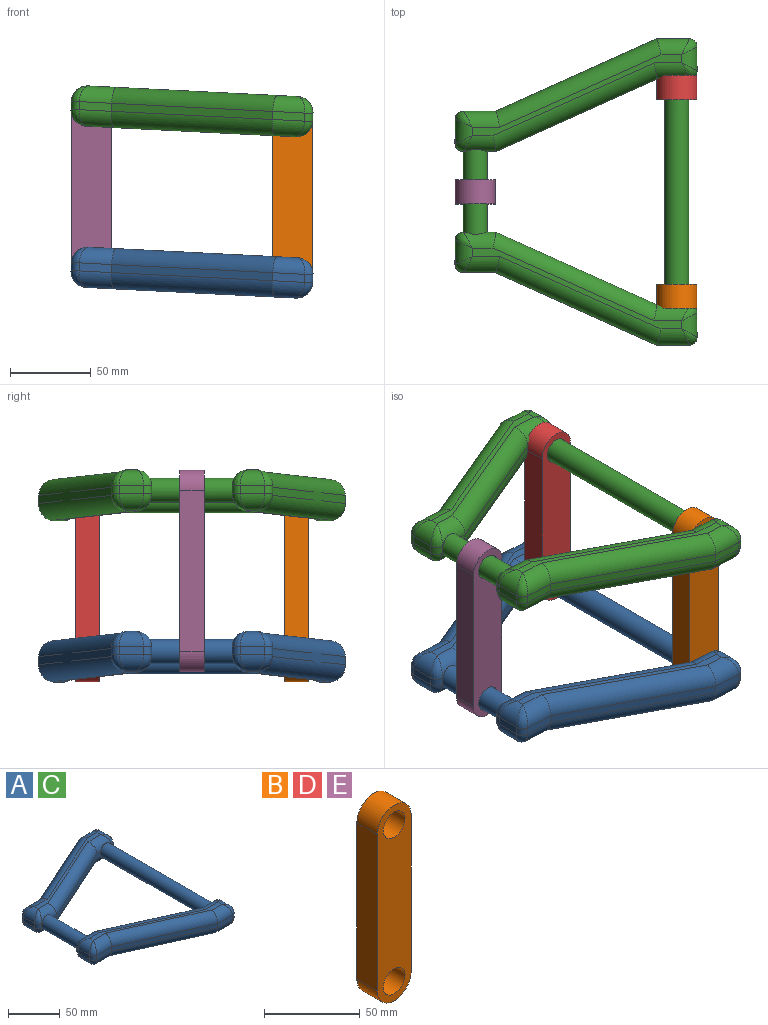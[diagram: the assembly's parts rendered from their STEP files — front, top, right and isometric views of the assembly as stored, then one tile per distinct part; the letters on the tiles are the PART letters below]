
ASSEMBLY  parts=5 mates=6
PART A: 86 faces, bbox 150x190x25 mm
  f0: plane 2.5x0.43mm, normal (0,1,0), area 0.4mm2, adj f18,f38,f84
  f1: plane 2.5x0.43mm, normal (0,1,0), area 0.4mm2, adj f19,f33,f78
  f2: plane 2.5x0.43mm, normal (0,-1,0), area 0.4mm2, adj f19,f51,f69
  f3: plane 2.5x0.43mm, normal (0,-1,0), area 0.4mm2, adj f18,f55,f63
  f4: plane 2.5x0.43mm, normal (0,-1,0), area 0.4mm2, adj f18,f47,f63
  f5: plane 5.43x5mm, normal (0,-1,0), area 25.7mm2, adj f12,f19,f51,f59
  f6: plane 2.5x0.43mm, normal (0,1,0), area 0.4mm2, adj f19,f41,f78
  f7: plane 2.5x0.43mm, normal (0,1,0), area 0.4mm2, adj f18,f37,f84
  f8: plane 100x45mm, normal (-0.41,0.91,0), area 548.3mm2, adj f9,f15,f50,f58
  f9: plane 20x5mm, normal (0,1,0), area 100mm2, adj f8,f48,f56,f66
  f10: plane 15x5mm, normal (-1,0,0), area 75mm2, adj f46,f54,f63,f66
  f11: plane 5.43x5mm, normal (0,-1,0), area 25.7mm2, adj f12,f18,f47,f55
  f12: plane 100x45mm, normal (0.41,-0.91,0), area 548.3mm2, adj f5,f11,f49,f57
  f13: plane 2.5x0.43mm, normal (0,-1,0), area 0.4mm2, adj f19,f59,f69
  f14: plane 15x5mm, normal (1,0,0), area 75mm2, adj f53,f61,f69,f72
  f15: plane 20x5mm, normal (0,1,0), area 100mm2, adj f8,f52,f60,f72
  f16: plane 130x50mm, normal (0,0,1), area 456.8mm2, adj f54,f55,f56,f57,f58,f59,f60,f61
  f17: plane 130x50mm, normal (0,0,-1), area 456.8mm2, adj f46,f47,f48,f49,f50,f51,f52,f53
  f18: cylinder r=7.5mm len=52.68mm, axis (0,1,0), area 2406.1mm2, adj f0,f3,f4,f7,f11,f23,f37,f38
  f19: cylinder r=7.5mm len=142.68mm, axis (0,1,0), area 6647.2mm2, adj f1,f2,f5,f6,f13,f25,f33,f41
  f20: plane 100x45mm, normal (-0.41,-0.91,0), area 548.3mm2, adj f21,f27,f32,f44
  f21: plane 20x5mm, normal (0,-1,0), area 100mm2, adj f20,f34,f42,f81
  f22: plane 15x5mm, normal (-1,0,0), area 75mm2, adj f36,f40,f81,f84
  f23: plane 5.43x5mm, normal (0,1,0), area 25.7mm2, adj f18,f24,f37,f38
  f24: plane 100x45mm, normal (0.41,0.91,0), area 548.3mm2, adj f23,f25,f35,f39
  f25: plane 5.43x5mm, normal (0,1,0), area 25.7mm2, adj f19,f24,f33,f41
  f26: plane 15x5mm, normal (1,0,0), area 75mm2, adj f31,f43,f75,f78
  f27: plane 20x5mm, normal (0,-1,0), area 100mm2, adj f20,f30,f45,f75
  f28: plane 130x50mm, normal (0,0,1), area 456.8mm2, adj f30,f31,f32,f33,f34,f35,f36,f37
  f29: plane 130x50mm, normal (0,0,-1), area 456.8mm2, adj f38,f39,f40,f41,f42,f43,f44,f45
  f30: cylinder r=10mm len=20mm, axis (1,0,0), area 273.4mm2, adj f27,f28,f32,f74
  f31: cylinder r=10mm len=15mm, axis (0,1,0), area 178.5mm2, adj f26,f28,f74,f77
  f32: cylinder r=10mm len=106.06mm, axis (0.91,-0.41,0), area 1722.5mm2, adj f20,f28,f30,f34
  f33: cylinder r=10mm len=22.15mm, axis (-1,0,0), area 244.6mm2, adj f1,f19,f25,f28,f35,f77
  f34: cylinder r=10mm len=22.15mm, axis (1,0,0), area 297.9mm2, adj f21,f28,f32,f80
  f35: cylinder r=10mm len=106.06mm, axis (-0.91,0.41,0), area 1722.5mm2, adj f24,f28,f33,f37
  f36: cylinder r=10mm len=15mm, axis (0,-1,0), area 178.5mm2, adj f22,f28,f80,f83
  f37: cylinder r=10mm len=20mm, axis (-1,0,0), area 220.1mm2, adj f7,f18,f23,f28,f35,f83
  f38: cylinder r=10mm len=20mm, axis (1,0,0), area 220.1mm2, adj f0,f18,f23,f29,f39,f85
  f39: cylinder r=10mm len=106.06mm, axis (0.91,-0.41,0), area 1722.5mm2, adj f24,f29,f38,f41
  f40: cylinder r=10mm len=15mm, axis (0,1,0), area 178.5mm2, adj f22,f29,f82,f85
  f41: cylinder r=10mm len=22.15mm, axis (1,0,0), area 244.6mm2, adj f6,f19,f25,f29,f39,f79
  f42: cylinder r=10mm len=22.15mm, axis (-1,0,0), area 297.9mm2, adj f21,f29,f44,f82
  f43: cylinder r=10mm len=15mm, axis (0,-1,0), area 178.5mm2, adj f26,f29,f76,f79
  f44: cylinder r=10mm len=106.06mm, axis (-0.91,0.41,0), area 1722.5mm2, adj f20,f29,f42,f45
  f45: cylinder r=10mm len=20mm, axis (-1,0,0), area 273.4mm2, adj f27,f29,f44,f76
  f46: cylinder r=10mm len=15mm, axis (0,-1,0), area 178.5mm2, adj f10,f17,f64,f67
  f47: cylinder r=10mm len=20mm, axis (1,0,0), area 220.1mm2, adj f4,f11,f17,f18,f49,f64
  f48: cylinder r=10mm len=22.15mm, axis (-1,0,0), area 297.9mm2, adj f9,f17,f50,f67
  f49: cylinder r=10mm len=106.06mm, axis (0.91,0.41,0), area 1722.5mm2, adj f12,f17,f47,f51
  f50: cylinder r=10mm len=106.06mm, axis (-0.91,-0.41,0), area 1722.5mm2, adj f8,f17,f48,f52
  f51: cylinder r=10mm len=22.15mm, axis (1,0,0), area 244.6mm2, adj f2,f5,f17,f19,f49,f70
  f52: cylinder r=10mm len=20mm, axis (-1,0,0), area 273.4mm2, adj f15,f17,f50,f73
  f53: cylinder r=10mm len=15mm, axis (0,1,0), area 178.5mm2, adj f14,f17,f70,f73
  f54: cylinder r=10mm len=15mm, axis (0,1,0), area 178.5mm2, adj f10,f16,f62,f65
  f55: cylinder r=10mm len=20mm, axis (-1,0,0), area 220.1mm2, adj f3,f11,f16,f18,f57,f62
  f56: cylinder r=10mm len=22.15mm, axis (1,0,0), area 297.9mm2, adj f9,f16,f58,f65
  f57: cylinder r=10mm len=106.06mm, axis (-0.91,-0.41,0), area 1722.5mm2, adj f12,f16,f55,f59
  f58: cylinder r=10mm len=106.06mm, axis (0.91,0.41,0), area 1722.5mm2, adj f8,f16,f56,f60
  f59: cylinder r=10mm len=22.15mm, axis (-1,0,0), area 244.6mm2, adj f5,f13,f16,f19,f57,f68
  f60: cylinder r=10mm len=20mm, axis (1,0,0), area 273.4mm2, adj f15,f16,f58,f71
  f61: cylinder r=10mm len=15mm, axis (0,-1,0), area 178.5mm2, adj f14,f16,f68,f71
  f62: bspline ~11.94x10mm, area 82.5mm2, adj f54,f55,f63
  f63: cylinder r=5mm len=5mm, axis (0,0,1), area 39.3mm2, adj f3,f4,f10,f62,f64
  f64: bspline ~11.94x10mm, area 82.5mm2, adj f46,f47,f63
  f65: bspline ~11.94x10mm, area 82.5mm2, adj f54,f56,f66
  f66: cylinder r=5mm len=5mm, axis (0,0,-1), area 39.3mm2, adj f9,f10,f65,f67
  f67: bspline ~11.94x10mm, area 82.5mm2, adj f46,f48,f66
  f68: bspline ~11.94x10mm, area 82.5mm2, adj f59,f61,f69
  f69: cylinder r=5mm len=5mm, axis (0,0,1), area 39.3mm2, adj f2,f13,f14,f68,f70
  f70: bspline ~11.94x10mm, area 82.5mm2, adj f51,f53,f69
  f71: bspline ~11.94x10mm, area 82.5mm2, adj f60,f61,f72
  f72: cylinder r=5mm len=5mm, axis (0,0,-1), area 39.3mm2, adj f14,f15,f71,f73
  f73: bspline ~11.94x10mm, area 82.5mm2, adj f52,f53,f72
  f74: bspline ~10.49x10mm, area 81.9mm2, adj f30,f31,f75
  f75: cylinder r=5mm len=5mm, axis (0,0,-1), area 39.3mm2, adj f26,f27,f74,f76
  f76: bspline ~10.49x10mm, area 81.9mm2, adj f43,f45,f75
  f77: bspline ~10.49x10mm, area 81.3mm2, adj f31,f33,f78
  f78: cylinder r=5mm len=5mm, axis (0,0,1), area 39.3mm2, adj f1,f6,f26,f77,f79
  f79: bspline ~10.49x10mm, area 81.9mm2, adj f41,f43,f78
  f80: bspline ~11.94x10mm, area 81.9mm2, adj f34,f36,f81
  f81: cylinder r=5mm len=5mm, axis (0,0,-1), area 39.3mm2, adj f21,f22,f80,f82
  f82: bspline ~11.94x10mm, area 81.9mm2, adj f40,f42,f81
  f83: bspline ~11.94x10mm, area 81.9mm2, adj f36,f37,f84
  f84: cylinder r=5mm len=5mm, axis (0,0,1), area 39.3mm2, adj f0,f7,f22,f83,f85
  f85: bspline ~11.94x10mm, area 81.9mm2, adj f38,f40,f84
PART B: 8 faces, bbox 25x15x125 mm
  f0: cylinder r=12.5mm len=25mm, axis (0,1,0), area 589mm2, adj f1,f5,f6,f7
  f1: plane 100x15mm, normal (-1,0,0), area 1500mm2, adj f0,f2,f6,f7
  f2: cylinder r=12.5mm len=25mm, axis (0,1,0), area 589mm2, adj f1,f5,f6,f7
  f3: cylinder r=8mm len=16mm, axis (0,1,0), area 754mm2, adj f6,f7
  f4: cylinder r=8mm len=16mm, axis (0,1,0), area 754mm2, adj f6,f7
  f5: plane 100x15mm, normal (1,0,0), area 1500mm2, adj f0,f2,f6,f7
  f6: plane 125x25mm, normal (0,-1,0), area 2588.7mm2, adj f0,f1,f2,f3,f4,f5
  f7: plane 125x25mm, normal (0,1,0), area 2588.7mm2, adj f0,f1,f2,f3,f4,f5
PART C: same geometry as A
PART D: same geometry as B
PART E: same geometry as B
PLACE A rot(axis=(0,1,0),2.9deg) t=(-77.49,-16.73,49.01)mm
PLACE B t=(-76.84,-81.45,49.63)mm fixed
PLACE C rot(axis=(0,1,0),2.9deg) t=(-77.49,-16.73,149.01)mm
PLACE D t=(-76.84,47.99,49.63)mm fixed
PLACE E t=(-201.68,-16.73,55.95)mm
MATE revolute D.f0 <-> C.f19  axis (0,1,0) through (-89.34,55.49,162.13)mm
MATE revolute B.f2 <-> A.f19  axis (0,1,0) through (-89.34,-88.95,62.13)mm
MATE revolute E.f0 <-> C.f18  axis (0,1,0) through (-214.18,-16.73,168.45)mm
MATE revolute D.f2 <-> A.f19  axis (0,1,0) through (-89.34,55.49,62.13)mm
MATE revolute B.f0 <-> C.f19  axis (0,-1,0) through (-89.34,-88.95,162.13)mm
MATE revolute E.f2 <-> A.f18  axis (0,1,0) through (-214.18,-16.73,68.45)mm
